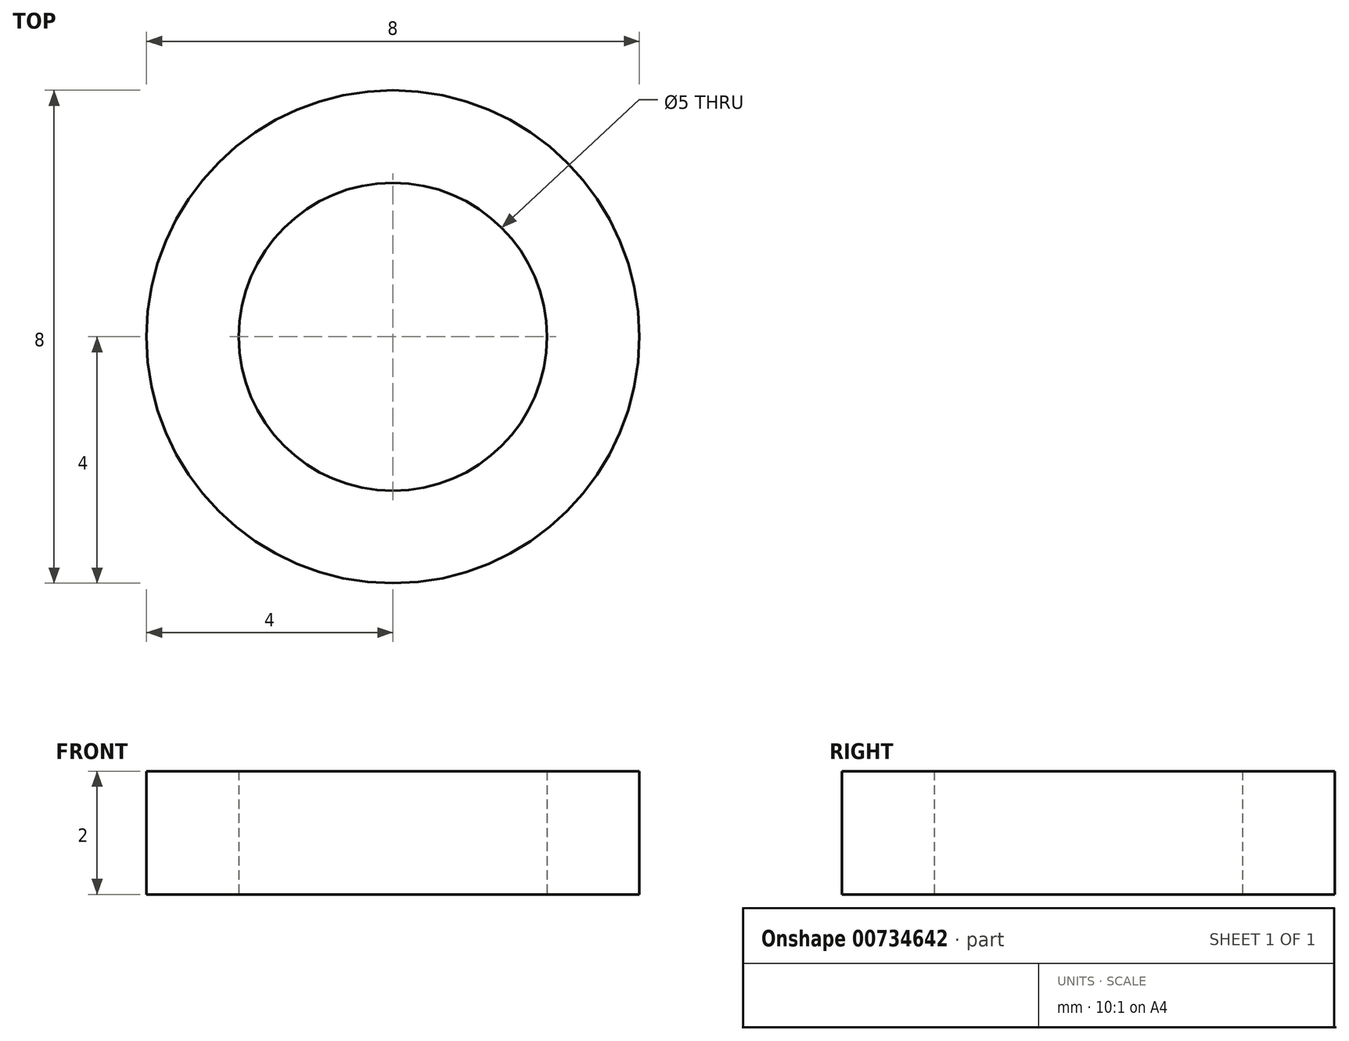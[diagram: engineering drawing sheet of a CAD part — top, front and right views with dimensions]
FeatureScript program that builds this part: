
annotation { "Feature Type Name" : "Feature", "Feature Type Description" : "" }
export const myFeature = defineFeature(function(context is Context, id is Id, definition is map)
    precondition{}
    {
        {
            var Q0;
            Q0=qCreatedBy(makeId("Top.planeOp"),FACE);
            var sketch = newSketch(context, id + "F0", { "sketchPlane" : qUnion([Q0])});
            skCircle(sketch, "E0", {"center": v(0, 0) * mm, "radius": 2.5 * mm});
            skCircle(sketch, "E1", {"center": v(0, 0) * mm, "radius": 4 * mm});
            skSolve(sketch);
        }
        {
            var Q0;
            Q0 = qSketchRegion(id + "F0", true);
            extrude(context, id + "F1", {"entities" : qUnion([Q0]), "depth" : 2 * mm, "offsetDistance" : 25 * mm});
        }
    });
